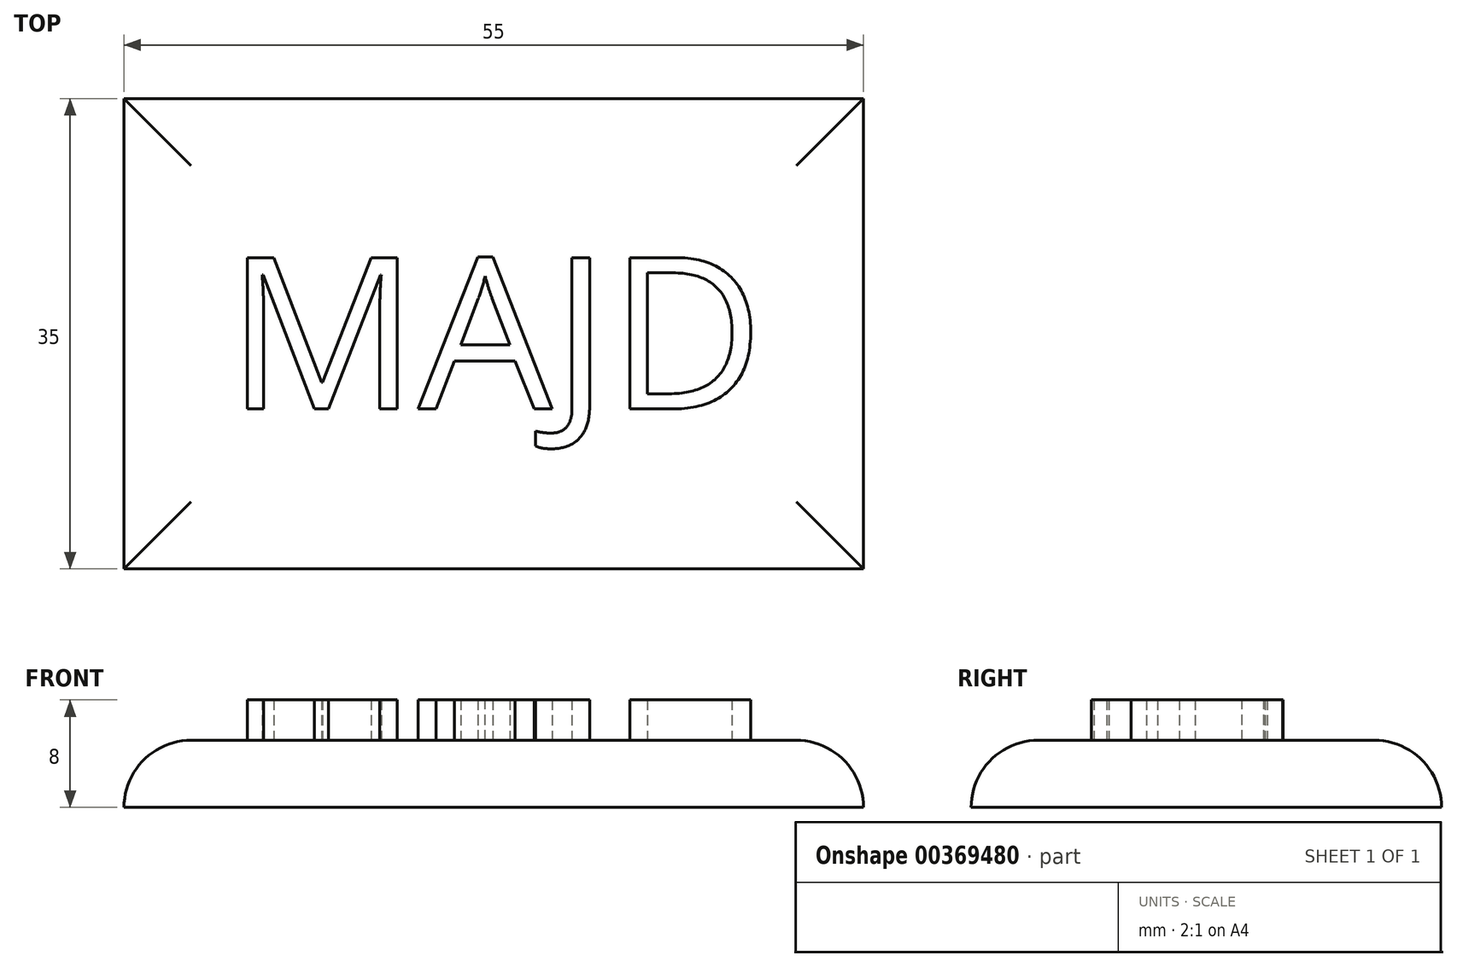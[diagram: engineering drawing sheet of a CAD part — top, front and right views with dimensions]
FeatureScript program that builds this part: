
annotation { "Feature Type Name" : "Feature", "Feature Type Description" : "" }
export const myFeature = defineFeature(function(context is Context, id is Id, definition is map)
    precondition{}
    {
        {
            var Q0;
            Q0=qCreatedBy(makeId("Top.planeOp"),FACE);
            var sketch = newSketch(context, id + "F0", { "sketchPlane" : qUnion([Q0])});
            skLineSegment(sketch, "E0.bottom", {"start": v(27.5, -17.5) * mm, "end": v(-27.5, -17.5) * mm});
            skLineSegment(sketch, "E0.top", {"start": v(27.5, 17.5) * mm, "end": v(-27.5, 17.5) * mm});
            skLineSegment(sketch, "E0.left", {"start": v(27.5, -17.5) * mm, "end": v(27.5, 17.5) * mm});
            skLineSegment(sketch, "E0.right", {"start": v(-27.5, -17.5) * mm, "end": v(-27.5, 17.5) * mm});
            skPoint(sketch, "E0.middle", {"position": v(0, 0) * mm});
            skSolve(sketch);
        }
        {
            var Q0;
            Q0=qSketchRegion(id+"F0",true);
            extrude(context, id + "F1", {"entities" : qUnion([Q0]), "depth" : 5 * mm});
        }
        {
            var Q0;
            Q0=makeQuery(id+"F1.opExtrude","CAP_EDGE",EDGE,{"disambiguationData":[OSD([sQuery(id+"F0.wireOp",EDGE,"E0.right")])],"isStart":false});
            var Q1;
            Q1=makeQuery(id+"F1.opExtrude","CAP_EDGE",EDGE,{"disambiguationData":[OSD([sQuery(id+"F0.wireOp",EDGE,"E0.left")])],"isStart":false});
            var Q2;
            Q2=makeQuery(id+"F1.opExtrude","CAP_EDGE",EDGE,{"disambiguationData":[OSD([sQuery(id+"F0.wireOp",EDGE,"E0.bottom")])],"isStart":false});
            var Q3;
            Q3=makeQuery(id+"F1.opExtrude","CAP_EDGE",EDGE,{"disambiguationData":[OSD([sQuery(id+"F0.wireOp",EDGE,"E0.top")])],"isStart":false});
            fillet(context, id + "F2", {"entities" : qUnion([Q0, Q1, Q2, Q3]), "radius" : 5 * mm, "tangentPropagation" : true, "allowEdgeOverflow" : false});
        }
        {
            var Q0;
            Q0=makeQuery(id+"F1.opExtrude","CAP_FACE",FACE,{"disambiguationData":[OSD([sQuery(id+"F0.wireOp",EDGE,"E0.bottom"),sQuery(id+"F0.wireOp",EDGE,"E0.top"),sQuery(id+"F0.wireOp",EDGE,"E0.left"),sQuery(id+"F0.wireOp",EDGE,"E0.right")])],"isStart":false});
            var sketch = newSketch(context, id + "F3", { "sketchPlane" : qUnion([Q0])});
            skText(sketch, "E1", { "text": "MAJD", "fontName": "OpenSans-Regular.ttf"});
            const initialGuessF3  = {"E1": [-0.01987, -0.0056, 1, 0, 0.01136]};
            skSetInitialGuess(sketch, initialGuessF3);
            skSolve(sketch);
        }
        {
            var Q0;
            Q0=qSketchRegion(id+"F3",true);
            extrude(context, id + "F4", {"entities" : qUnion([Q0]), "operationType" : NewBodyOperationType.ADD, "depth" : 3 * mm});
        }
    });
